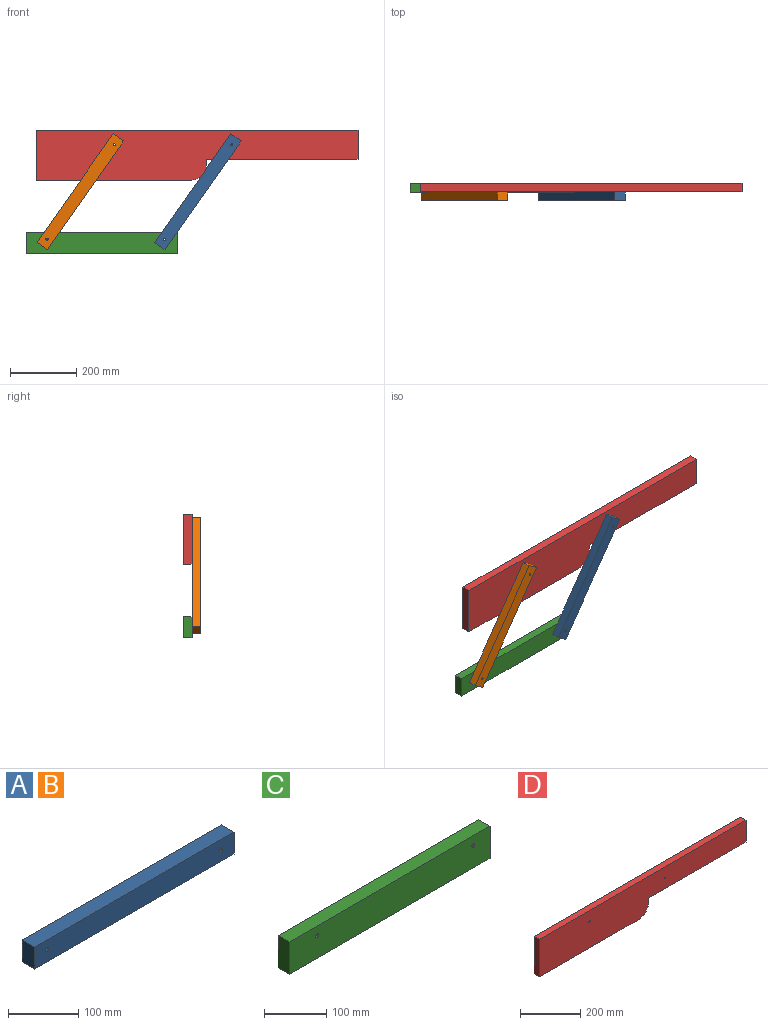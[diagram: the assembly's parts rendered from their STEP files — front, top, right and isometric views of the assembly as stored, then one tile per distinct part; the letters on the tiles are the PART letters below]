
ASSEMBLY  parts=4 mates=7
PART A: 8 faces, bbox 401.3x25.4x38.1 mm
  f0: plane 401.32x25.4mm, normal (0,0,1), area 10193.5mm2, adj f1,f5,f6,f7
  f1: plane 38.1x25.4mm, normal (-1,0,0), area 967.7mm2, adj f0,f2,f6,f7
  f2: plane 401.32x25.4mm, normal (0,0,-1), area 10193.5mm2, adj f1,f5,f6,f7
  f3: cylinder r=3.17mm len=25.4mm, axis (0,1,0), area 506.7mm2, adj f6,f7
  f4: cylinder r=3.17mm len=25.4mm, axis (0,1,0), area 506.7mm2, adj f6,f7
  f5: plane 38.1x25.4mm, normal (1,0,0), area 967.7mm2, adj f0,f2,f6,f7
  f6: plane 401.32x38.1mm, normal (0,-1,0), area 15227mm2, adj f0,f1,f2,f3,f4,f5
  f7: plane 401.32x38.1mm, normal (0,1,0), area 15227mm2, adj f0,f1,f2,f3,f4,f5
PART B: same geometry as A
PART C: 8 faces, bbox 457.2x25.4x63.5 mm
  f0: plane 457.2x25.4mm, normal (0,0,1), area 11612.9mm2, adj f1,f3,f4,f5
  f1: plane 63.5x25.4mm, normal (-1,0,0), area 1612.9mm2, adj f0,f2,f4,f5
  f2: plane 457.2x25.4mm, normal (0,0,-1), area 11612.9mm2, adj f1,f3,f4,f5
  f3: plane 63.5x25.4mm, normal (1,0,0), area 1612.9mm2, adj f0,f2,f4,f5
  f4: plane 457.2x63.5mm, normal (0,-1,0), area 28968.9mm2, adj f0,f1,f2,f3,f6,f7
  f5: plane 457.2x63.5mm, normal (0,1,0), area 28968.9mm2, adj f0,f1,f2,f3,f6,f7
  f6: cylinder r=3.17mm len=25.4mm, axis (0,-1,0), area 506.7mm2, adj f4,f5
  f7: cylinder r=3.17mm len=25.4mm, axis (0,-1,0), area 506.7mm2, adj f4,f5
PART D: 11 faces, bbox 972.2x25.4x152.4 mm
  f0: plane 972.16x25.4mm, normal (0,0,1), area 24692.9mm2, adj f1,f5,f6,f7
  f1: plane 152.4x25.4mm, normal (-1,0,0), area 3871mm2, adj f0,f2,f6,f7
  f2: plane 464.16x25.4mm, normal (0,0,-1), area 11789.7mm2, adj f1,f6,f7,f10
  f3: plane 25.4x12.7mm, normal (1,0,0), area 322.6mm2, adj f4,f6,f7,f10
  f4: plane 457.2x25.4mm, normal (0,0,-1), area 11612.9mm2, adj f3,f5,f6,f7
  f5: plane 88.9x25.4mm, normal (1,0,0), area 2258.1mm2, adj f0,f4,f6,f7
  f6: plane 972.16x152.4mm, normal (0,-1,0), area 118508.3mm2, adj f0,f1,f2,f3,f4,f5,f8,f9
  f7: plane 972.16x152.4mm, normal (0,1,0), area 118508.3mm2, adj f0,f1,f2,f3,f4,f5,f8,f9
  f8: cylinder r=3.17mm len=25.4mm, axis (0,-1,0), area 506.7mm2, adj f6,f7
  f9: cylinder r=3.17mm len=25.4mm, axis (0,-1,0), area 506.7mm2, adj f6,f7
  f10: cylinder r=50.8mm len=50.8mm, axis (0,1,0), area 2026.8mm2, adj f2,f3,f6,f7
PLACE A rot(axis=(0,1,0),125deg) t=(-19.81,-35.61,-9.58)mm
PLACE B rot(axis=(0,1,0),125deg) t=(-375.41,-35.61,-9.58)mm
PLACE C t=(-29.39,-10.21,-297.46)mm
PLACE D t=(-49.56,-10.21,21.08)mm fixed
MATE revolute B.f3 <-> C.f6  axis (0,1,0) through (-520.74,-35.61,-230.23)mm
MATE revolute D.f8 <-> B.f4  axis (0,-1,0) through (-317.42,-35.61,55.32)mm
MATE revolute A.f3 <-> C.f7  axis (0,1,0) through (-165.14,-35.61,-230.23)mm
MATE revolute D.f9 <-> A.f4  axis (0,-1,0) through (38.18,-35.61,55.32)mm
MATE planar D.f6 <-> B.f4  axis (0,-1,0) through (-130.02,-35.61,34.74)mm
MATE planar C.f4 <-> B.f7  axis (0,-1,0) through (-355.66,-35.61,-242.95)mm
MATE planar A.f7 <-> D.f6  axis (0,1,0) through (-64.59,-35.61,-86.68)mm
